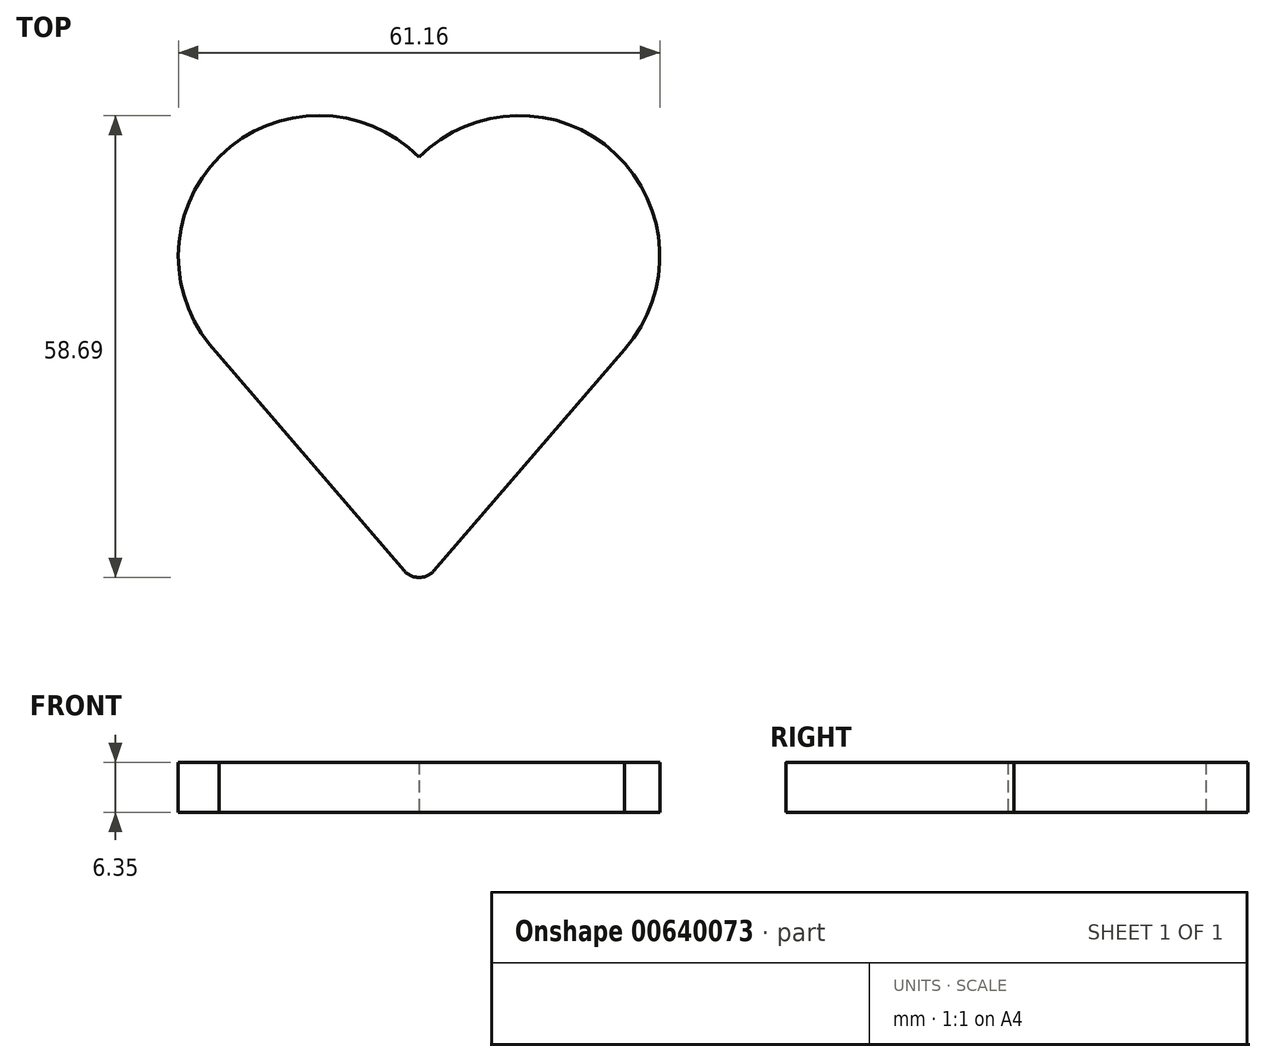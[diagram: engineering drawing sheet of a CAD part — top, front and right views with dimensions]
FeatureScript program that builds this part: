
annotation { "Feature Type Name" : "Feature", "Feature Type Description" : "" }
export const myFeature = defineFeature(function(context is Context, id is Id, definition is map)
    precondition{}
    {
        {
            var Q0;
            Q0=qCreatedBy(makeId("Top.planeOp"), FACE);
            var sketch = newSketch(context, id + "F0", { "sketchPlane" : qUnion([Q0])});
            skLineSegment(sketch, "E0", {"start": v(-26.11, 67.31) * mm, "end": v(-26.11, 3.81) * mm});
            skLineSegment(sketch, "E1", {"start": v(-51.51, 45.98) * mm, "end": v(-0.71, 45.98) * mm});
            skPoint(sketch, "E2", {"position": v(-26.11, 45.98) * mm});
            skPoint(sketch, "E3", {"position": v(-38.81, 45.98) * mm});
            skPoint(sketch, "E4", {"position": v(-13.41, 45.98) * mm});
            skArc(sketch, "E5", {"start": v(-26.11, 58.56) * mm, "mid": v(-51.4, 58.68) * mm, "end": v(-51.51, 33.4) * mm});
            skArc(sketch, "E6", {"start": v(-26.11, 58.56) * mm, "mid": v(-1.2, 59.04) * mm, "end": v(0, 34.16) * mm});
            skLineSegment(sketch, "E7", {"start": v(-51.51, 33.4) * mm, "end": v(-26.11, 3.81) * mm});
            skLineSegment(sketch, "E8", {"start": v(0, 34.16) * mm, "end": v(-26.11, 3.81) * mm});
            skSolve(sketch);
        }
        {
            var Q0;
            Q0 = qSketchRegion(id + "F0", true);
            extrude(context, id + "F1", {"entities" : qUnion([Q0]), "depth" : 6.35 * mm, "offsetDistance" : 25.4 * mm});
        }
        {
            var Q0;
            Q0=makeQuery(id+"F1.opExtrude","SWEPT_EDGE",EDGE,{"disambiguationData":[OSD([sQuery(id+"F0.wireOp",EDGE,"E0"),sQuery(id+"F0.wireOp",EDGE,"E7"),sQuery(id+"F0.wireOp",EDGE,"E8")])]});
            fillet(context, id + "F2", {"entities" : qUnion([Q0]), "radius" : 2.54 * mm, "tangentPropagation" : true, "allowEdgeOverflow" : false});
        }
    });
